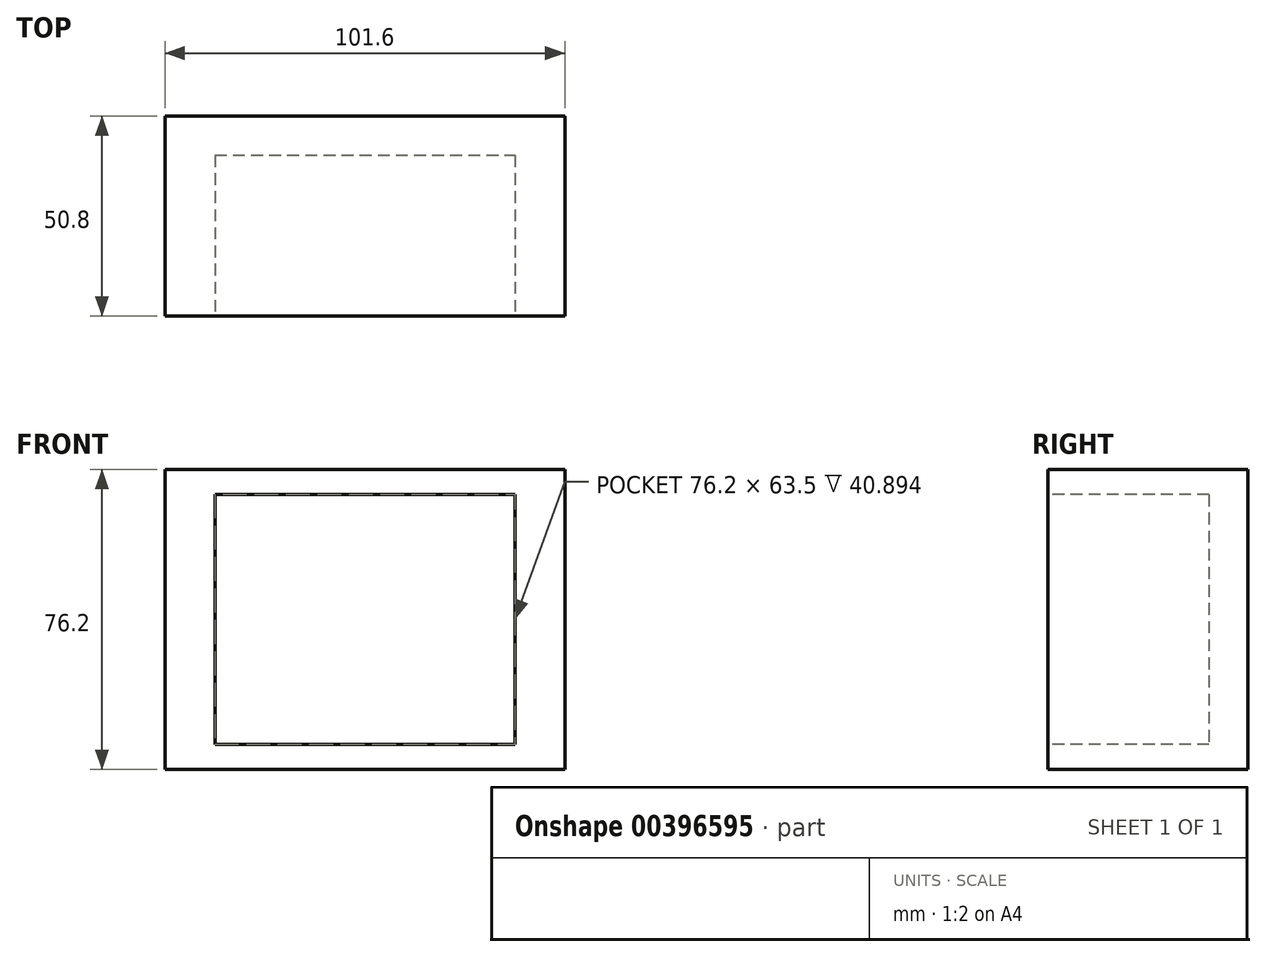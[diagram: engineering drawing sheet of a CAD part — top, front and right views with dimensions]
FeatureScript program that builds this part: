
annotation { "Feature Type Name" : "Feature", "Feature Type Description" : "" }
export const myFeature = defineFeature(function(context is Context, id is Id, definition is map)
    precondition{}
    {
        {
            var Q0;
            Q0=qCreatedBy(makeId("Front.planeOp"),FACE);
            var sketch = newSketch(context, id + "F0", { "sketchPlane" : qUnion([Q0])});
            skLineSegment(sketch, "E0.bottom", {"start": v(50.8, 38.1) * mm, "end": v(-50.8, 38.1) * mm});
            skLineSegment(sketch, "E0.top", {"start": v(50.8, -38.1) * mm, "end": v(-50.8, -38.1) * mm});
            skLineSegment(sketch, "E0.left", {"start": v(50.8, 38.1) * mm, "end": v(50.8, -38.1) * mm});
            skLineSegment(sketch, "E0.right", {"start": v(-50.8, 38.1) * mm, "end": v(-50.8, -38.1) * mm});
            skPoint(sketch, "E0.middle", {"position": v(0, 0) * mm});
            skLineSegment(sketch, "E1.bottom", {"start": v(-38.1, 31.75) * mm, "end": v(38.1, 31.75) * mm});
            skLineSegment(sketch, "E1.top", {"start": v(-38.1, -31.75) * mm, "end": v(38.1, -31.75) * mm});
            skLineSegment(sketch, "E1.left", {"start": v(-38.1, 31.75) * mm, "end": v(-38.1, -31.75) * mm});
            skLineSegment(sketch, "E1.right", {"start": v(38.1, 31.75) * mm, "end": v(38.1, -31.75) * mm});
            skSolve(sketch);
        }
        {
            var Q0;
            Q0=makeQuery(id+"F0.imprint","IMPRINT",FACE,{"disambiguationData":[TD([[makeQuery(id+"F0.imprint","IMPRINT",EDGE,{"derivedFrom":sQuery(id+"F0.wireOp",EDGE,"E0.bottom")}),1.0]])]});
            extrude(context, id + "F1", {"entities" : qUnion([Q0]), "oppositeDirection" : true, "depth" : 50.8 * mm});
        }
        {
            var Q0;
            Q0=makeQuery(id+"F1.opExtrude","CAP_FACE",FACE,{"disambiguationData":[OSD([sQuery(id+"F0.wireOp",EDGE,"E0.bottom"),sQuery(id+"F0.wireOp",EDGE,"E0.top"),sQuery(id+"F0.wireOp",EDGE,"E0.left"),sQuery(id+"F0.wireOp",EDGE,"E0.right"),sQuery(id+"F0.wireOp",EDGE,"E1.bottom"),sQuery(id+"F0.wireOp",EDGE,"E1.top"),sQuery(id+"F0.wireOp",EDGE,"E1.left"),sQuery(id+"F0.wireOp",EDGE,"E1.right")])],"isStart":false});
            var sketch = newSketch(context, id + "F2", { "sketchPlane" : qUnion([Q0])});
            skLineSegment(sketch, "E2.bottom", {"start": v(-38.1, 31.75) * mm, "end": v(38.1, 31.75) * mm});
            skLineSegment(sketch, "E2.top", {"start": v(-38.1, -31.75) * mm, "end": v(38.1, -31.75) * mm});
            skLineSegment(sketch, "E2.left", {"start": v(-38.1, 31.75) * mm, "end": v(-38.1, -31.75) * mm});
            skLineSegment(sketch, "E2.right", {"start": v(38.1, 31.75) * mm, "end": v(38.1, -31.75) * mm});
            skPoint(sketch, "E2.middle", {"position": v(0, 0) * mm});
            skSolve(sketch);
        }
        {
            var Q0;
            Q0=makeQuery(id+"F2.imprint","IMPRINT",FACE,{"disambiguationData":[TD([[makeQuery(id+"F2.imprint","IMPRINT",EDGE,{"derivedFrom":sQuery(id+"F2.wireOp",EDGE,"E2.bottom")}),1.0]])]});
            extrude(context, id + "F3", {"entities" : qUnion([Q0]), "operationType" : NewBodyOperationType.ADD, "oppositeDirection" : true, "depth" : 9.9 * mm});
        }
    });
